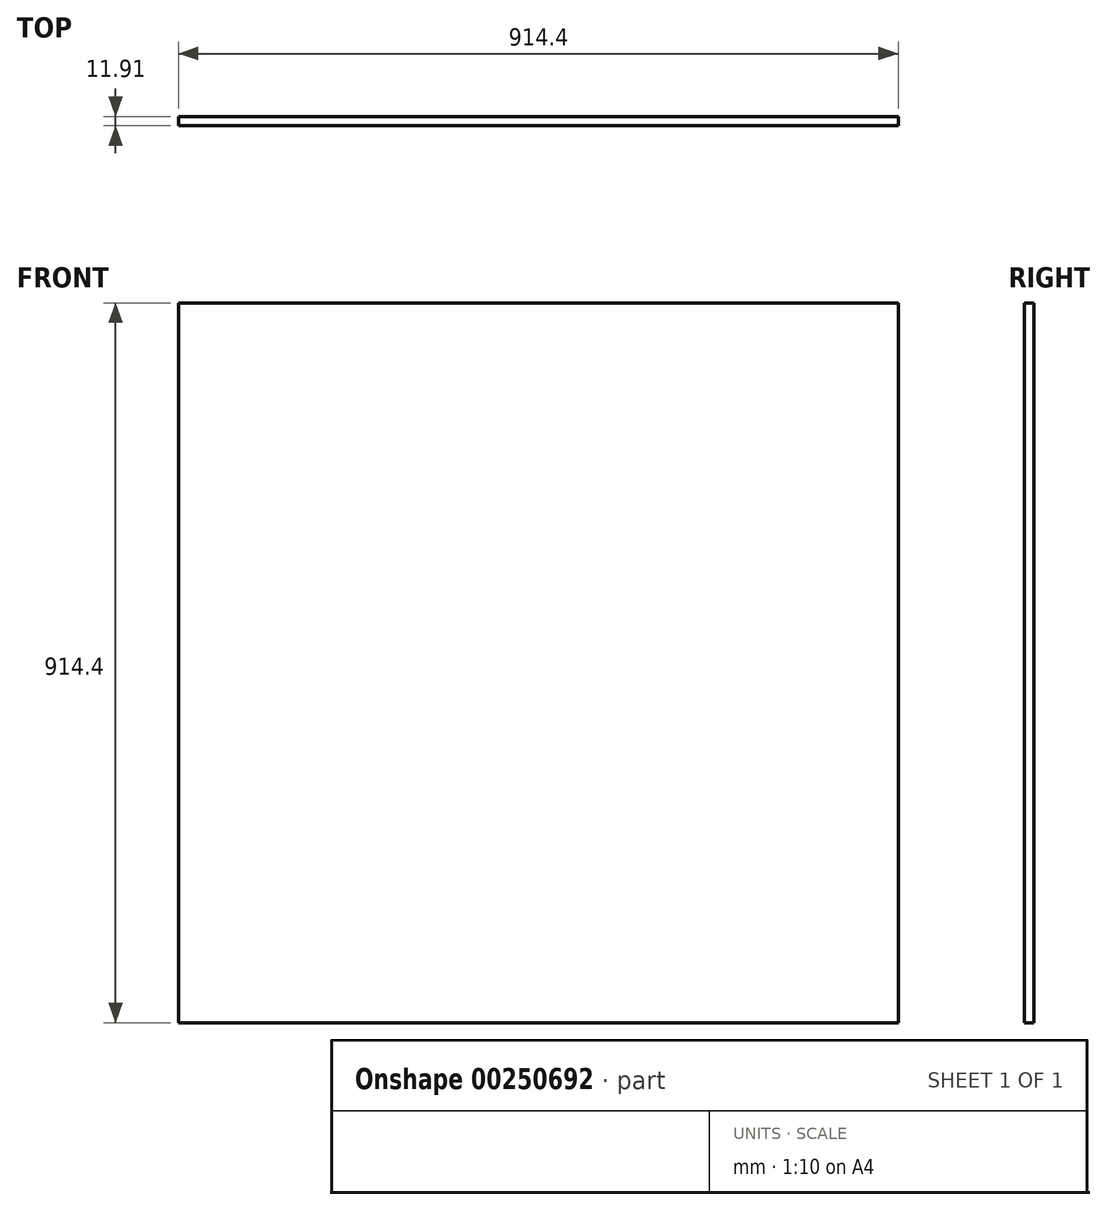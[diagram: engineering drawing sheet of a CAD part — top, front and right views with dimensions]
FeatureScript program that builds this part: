
annotation { "Feature Type Name" : "Feature", "Feature Type Description" : "" }
export const myFeature = defineFeature(function(context is Context, id is Id, definition is map)
    precondition{}
    {
        {
            var Q0;
            Q0=qCreatedBy(makeId("Front.planeOp"),FACE);
            var sketch = newSketch(context, id + "F0", { "sketchPlane" : qUnion([Q0])});
            skLineSegment(sketch, "E0.bottom", {"start": v(0, 0) * mm, "end": v(914.4, 0) * mm});
            skLineSegment(sketch, "E0.top", {"start": v(0, 914.4) * mm, "end": v(914.4, 914.4) * mm});
            skLineSegment(sketch, "E0.left", {"start": v(0, 0) * mm, "end": v(0, 914.4) * mm});
            skLineSegment(sketch, "E0.right", {"start": v(914.4, 0) * mm, "end": v(914.4, 914.4) * mm});
            skSolve(sketch);
        }
        {
            var Q0;
            Q0 = qSketchRegion(id + "F0", true);
            extrude(context, id + "F1", {"entities" : qUnion([Q0]), "depth" : 11.9 * mm});
        }
    });
